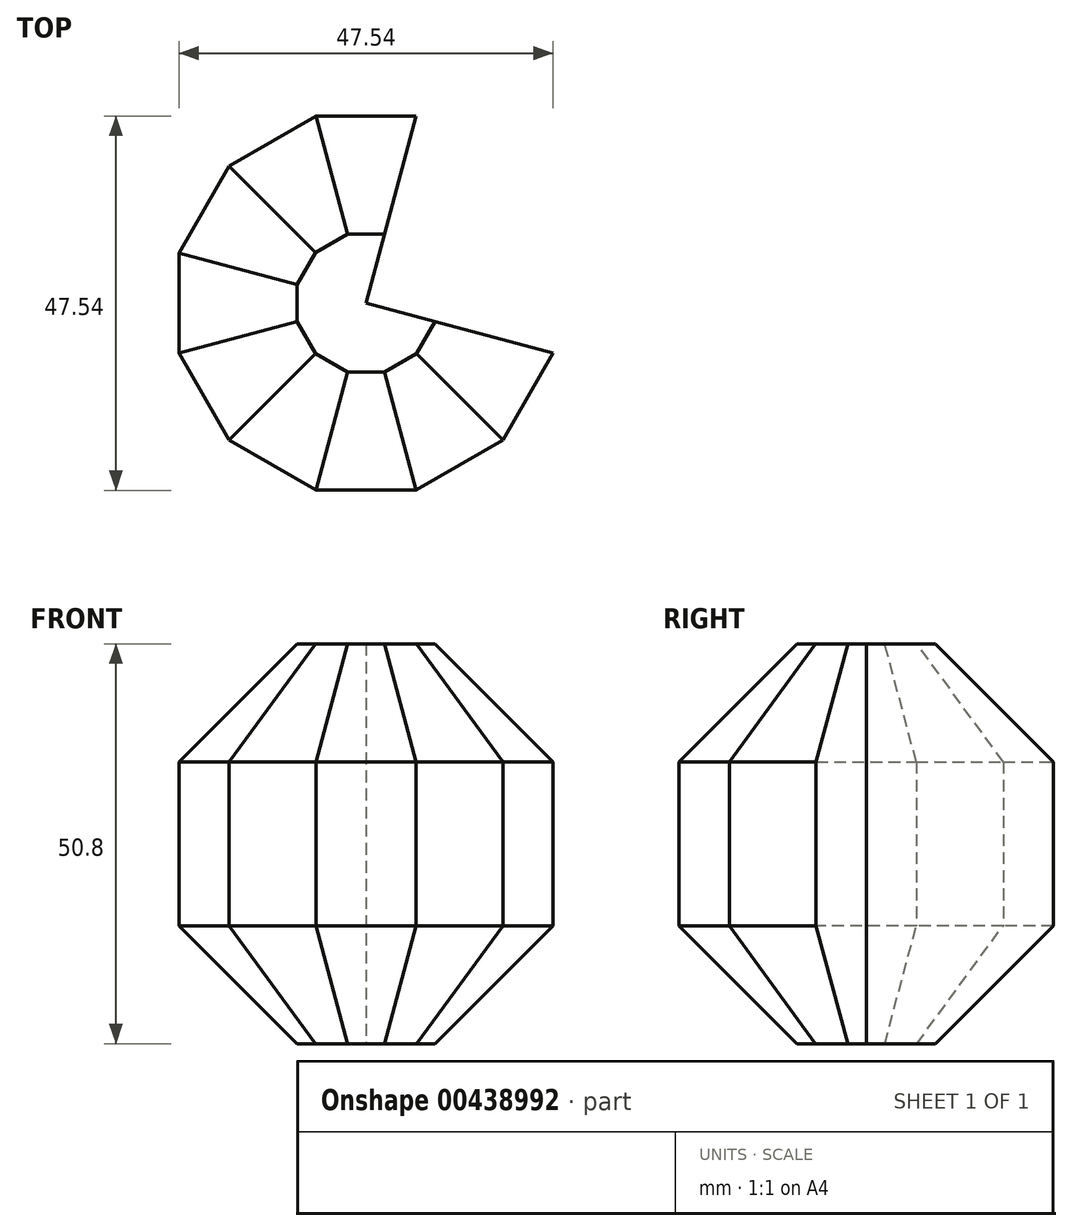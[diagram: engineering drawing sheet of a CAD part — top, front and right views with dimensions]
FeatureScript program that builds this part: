
annotation { "Feature Type Name" : "Feature", "Feature Type Description" : "" }
export const myFeature = defineFeature(function(context is Context, id is Id, definition is map)
    precondition{}
    {
        {
            var Q0;
            Q0=qCreatedBy(makeId("Top.planeOp"),FACE);
            var sketch = newSketch(context, id + "F0", { "sketchPlane" : qUnion([Q0])});
            skLineSegment(sketch, "E0.0", {"start": v(6.37, -23.77) * mm, "end": v(-6.37, -23.77) * mm});
            skLineSegment(sketch, "E0.1", {"start": v(-6.37, -23.77) * mm, "end": v(-17.4, -17.4) * mm});
            skLineSegment(sketch, "E0.2", {"start": v(-17.4, -17.4) * mm, "end": v(-23.77, -6.37) * mm});
            skLineSegment(sketch, "E0.3", {"start": v(-23.77, -6.37) * mm, "end": v(-23.77, 6.37) * mm});
            skLineSegment(sketch, "E0.4", {"start": v(-23.77, 6.37) * mm, "end": v(-17.4, 17.4) * mm});
            skLineSegment(sketch, "E0.5", {"start": v(-17.4, 17.4) * mm, "end": v(-6.37, 23.77) * mm});
            skLineSegment(sketch, "E0.6", {"start": v(-6.37, 23.77) * mm, "end": v(6.37, 23.77) * mm});
            skLineSegment(sketch, "E0.10", {"start": v(23.77, -6.37) * mm, "end": v(17.4, -17.4) * mm});
            skLineSegment(sketch, "E0.11", {"start": v(17.4, -17.4) * mm, "end": v(6.37, -23.77) * mm});
            skPoint(sketch, "E0.0.midPoint", {"position": v(0, -23.77) * mm});
            skLineSegment(sketch, "E1", {"start": v(6.37, 23.77) * mm, "end": v(0, 0) * mm});
            skLineSegment(sketch, "E2", {"start": v(0, 0) * mm, "end": v(23.77, -6.37) * mm});
            skSolve(sketch);
        }
        {
            var Q0;
            Q0=makeQuery(id+"F0.imprint","IMPRINT",FACE,{"disambiguationData":[TD([[makeQuery(id+"F0.imprint","IMPRINT",EDGE,{"derivedFrom":sQuery(id+"F0.wireOp",EDGE,"E0.0")}),-1.0]])]});
            extrude(context, id + "F1", {"entities" : qUnion([Q0]), "depth" : 50.8 * mm, "offsetDistance" : 25.4 * mm});
        }
        {
            var Q0;
            Q0=makeQuery(id+"F1.opExtrude","CAP_EDGE",EDGE,{"disambiguationData":[OSD([sQuery(id+"F0.wireOp",EDGE,"E0.6")])],"isStart":false});
            var Q1;
            Q1=makeQuery(id+"F1.opExtrude","CAP_EDGE",EDGE,{"disambiguationData":[OSD([sQuery(id+"F0.wireOp",EDGE,"E0.5")])],"isStart":false});
            var Q2;
            Q2=makeQuery(id+"F1.opExtrude","CAP_EDGE",EDGE,{"disambiguationData":[OSD([sQuery(id+"F0.wireOp",EDGE,"E0.4")])],"isStart":false});
            var Q3;
            Q3=makeQuery(id+"F1.opExtrude","CAP_EDGE",EDGE,{"disambiguationData":[OSD([sQuery(id+"F0.wireOp",EDGE,"E0.3")])],"isStart":false});
            var Q4;
            Q4=makeQuery(id+"F1.opExtrude","CAP_EDGE",EDGE,{"disambiguationData":[OSD([sQuery(id+"F0.wireOp",EDGE,"E0.2")])],"isStart":false});
            var Q5;
            Q5=makeQuery(id+"F1.opExtrude","CAP_EDGE",EDGE,{"disambiguationData":[OSD([sQuery(id+"F0.wireOp",EDGE,"E0.1")])],"isStart":false});
            var Q6;
            Q6=makeQuery(id+"F1.opExtrude","CAP_EDGE",EDGE,{"disambiguationData":[OSD([sQuery(id+"F0.wireOp",EDGE,"E0.6")])],"isStart":true});
            var Q7;
            Q7=makeQuery(id+"F1.opExtrude","CAP_EDGE",EDGE,{"disambiguationData":[OSD([sQuery(id+"F0.wireOp",EDGE,"E0.5")])],"isStart":true});
            var Q8;
            Q8=makeQuery(id+"F1.opExtrude","CAP_EDGE",EDGE,{"disambiguationData":[OSD([sQuery(id+"F0.wireOp",EDGE,"E0.4")])],"isStart":true});
            var Q9;
            Q9=makeQuery(id+"F1.opExtrude","CAP_EDGE",EDGE,{"disambiguationData":[OSD([sQuery(id+"F0.wireOp",EDGE,"E0.3")])],"isStart":true});
            var Q10;
            Q10=makeQuery(id+"F1.opExtrude","CAP_EDGE",EDGE,{"disambiguationData":[OSD([sQuery(id+"F0.wireOp",EDGE,"E0.2")])],"isStart":true});
            var Q11;
            Q11=makeQuery(id+"F1.opExtrude","CAP_EDGE",EDGE,{"disambiguationData":[OSD([sQuery(id+"F0.wireOp",EDGE,"E0.1")])],"isStart":true});
            var Q12;
            Q12=makeQuery(id+"F1.opExtrude","CAP_EDGE",EDGE,{"disambiguationData":[OSD([sQuery(id+"F0.wireOp",EDGE,"E0.10")])],"isStart":true});
            var Q13;
            Q13=makeQuery(id+"F1.opExtrude","CAP_EDGE",EDGE,{"disambiguationData":[OSD([sQuery(id+"F0.wireOp",EDGE,"E0.11")])],"isStart":true});
            var Q14;
            Q14=makeQuery(id+"F1.opExtrude","CAP_EDGE",EDGE,{"disambiguationData":[OSD([sQuery(id+"F0.wireOp",EDGE,"E0.0")])],"isStart":true});
            var Q15;
            Q15=makeQuery(id+"F1.opExtrude","CAP_EDGE",EDGE,{"disambiguationData":[OSD([sQuery(id+"F0.wireOp",EDGE,"E0.10")])],"isStart":false});
            var Q16;
            Q16=makeQuery(id+"F1.opExtrude","CAP_EDGE",EDGE,{"disambiguationData":[OSD([sQuery(id+"F0.wireOp",EDGE,"E0.11")])],"isStart":false});
            var Q17;
            Q17=makeQuery(id+"F1.opExtrude","CAP_EDGE",EDGE,{"disambiguationData":[OSD([sQuery(id+"F0.wireOp",EDGE,"E0.0")])],"isStart":false});
            chamfer(context, id + "F2", {"entities" : qUnion([Q0, Q1, Q2, Q3, Q4, Q5, Q6, Q7, Q8, Q9, Q10, Q11, Q12, Q13, Q14, Q15, Q16, Q17]), "width" : 15 * mm, "tangentPropagation" : true});
        }
    });
